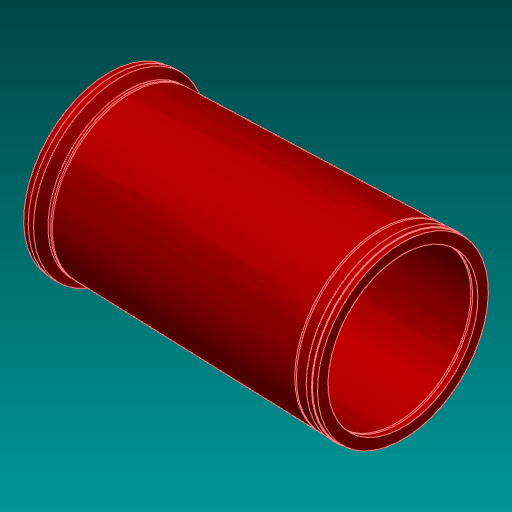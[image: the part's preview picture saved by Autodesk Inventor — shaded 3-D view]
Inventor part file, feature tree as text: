
AUTODESK INVENTOR PART (.ipt)
format: ipt  version: 2017.3 (Build 213257000, 257)  size: 241,152 bytes
history: native  units: in
note: dims shown in document units (in); Inventor stores cm internally (conversion verified against a paired STEP export)
features: revolve x1, fillet x1, sketch x1
ambient origin geometry x8: Origin, YZ Plane, XZ Plane, XY Plane, X Axis, Y Axis, Z Axis, Center Point
bodies: Solid1 (feature_tree)
feature tree (3):
  revolve  "Revolution1"  [1 undecoded]
  fillet  "Fillet1"  Radius=28.5in
  sketch  "Sketch1"  dims[d0=55.8661in d1=26.0in d2=28.5in d3=32.48in d4=2.0in d5=1.0in d6=1.0in d7=32.48in d8=30.0in d9=1.0in d10=4.0in d11=12.0in d12=12.0in d13=48.0in d14=2.0779in d15=90.0deg d16=0.0312in d17=1.0in d18=45.0deg d19=32.75in d23=1.0in d24=45.0deg d25=32.75in]
note: 1 required parameter value undecoded (feature->parameter linkage not recoverable at this tier; creation-order binding heuristic only, values carry confidence <= 0.55)
